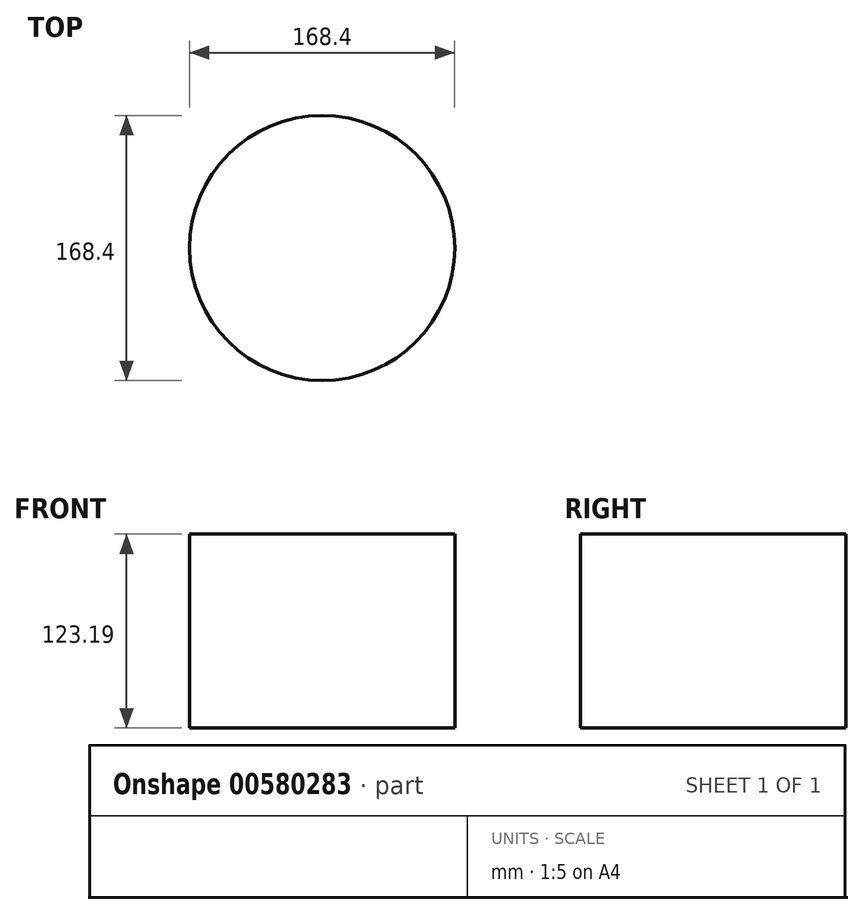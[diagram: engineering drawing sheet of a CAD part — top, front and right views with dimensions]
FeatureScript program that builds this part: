
annotation { "Feature Type Name" : "Feature", "Feature Type Description" : "" }
export const myFeature = defineFeature(function(context is Context, id is Id, definition is map)
    precondition{}
    {
        {
            var Q0;
            Q0=qCreatedBy(makeId("Top.planeOp"),FACE);
            var sketch = newSketch(context, id + "F0", { "sketchPlane" : qUnion([Q0])});
            skCircle(sketch, "E0", {"center": v(0, 0) * mm, "radius": 84.2 * mm});
            skSolve(sketch);
        }
        {
            var Q0;
            Q0=makeQuery(id+"F0.imprint","IMPRINT",FACE,{"disambiguationData":[TD([[makeQuery(id+"F0.imprint","IMPRINT",EDGE,{"derivedFrom":sQuery(id+"F0.wireOp",EDGE,"E0")}),1.0]])]});
            extrude(context, id + "F1", {"entities" : qUnion([Q0]), "depth" : 123.19 * mm, "offsetDistance" : 25.4 * mm});
        }
    });
